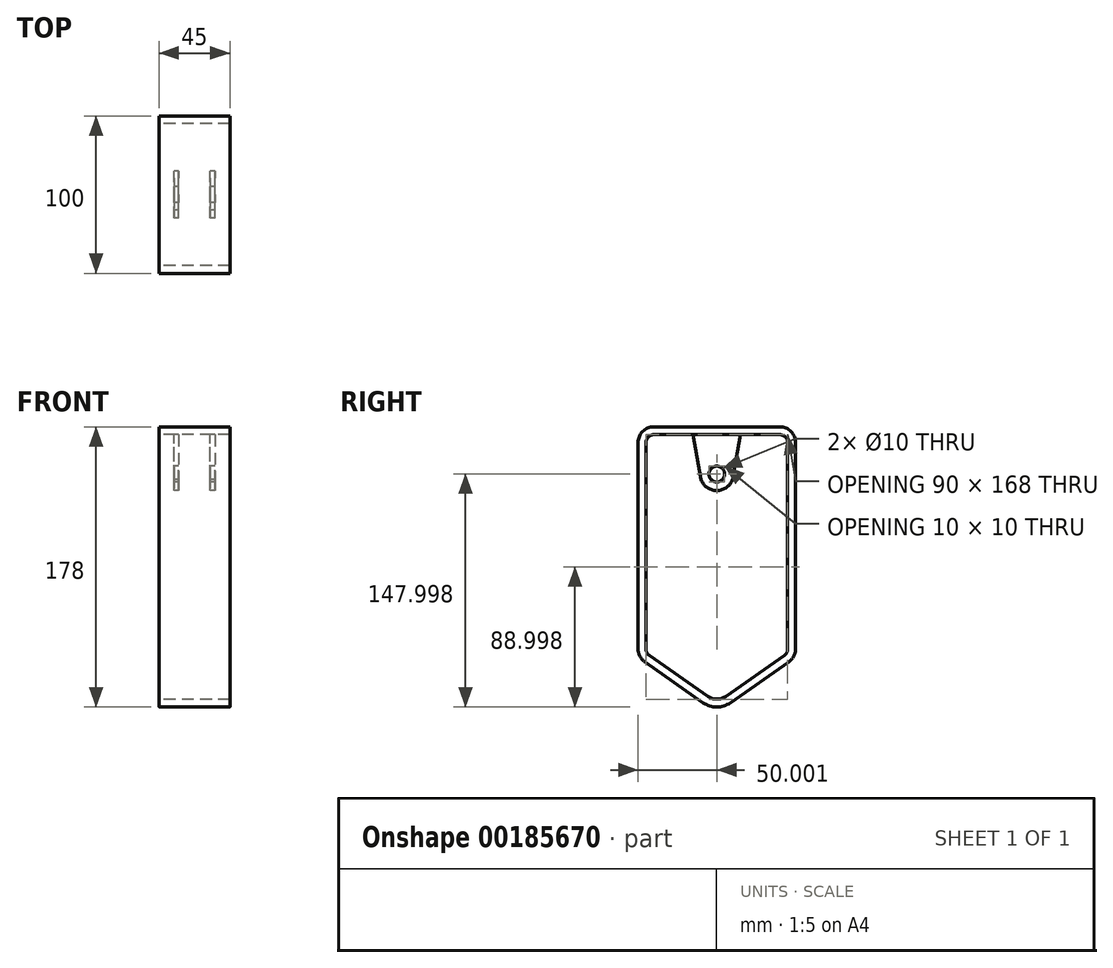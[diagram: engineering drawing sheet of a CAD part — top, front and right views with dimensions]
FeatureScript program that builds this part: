
annotation { "Feature Type Name" : "Feature", "Feature Type Description" : "" }
export const myFeature = defineFeature(function(context is Context, id is Id, definition is map)
    precondition{}
    {
        {
            var Q0;
            Q0=qCreatedBy(makeId("Right.planeOp"),FACE);
            var sketch = newSketch(context, id + "F0", { "sketchPlane" : qUnion([Q0])});
            skArc(sketch, "E0", {"start": v(-8.36, -11.33) * mm, "mid": v(0.24, -14.04) * mm, "end": v(8.84, -11.33) * mm});
            skArc(sketch, "E1", {"start": v(-5.5, -7.23) * mm, "mid": v(0.24, -9.04) * mm, "end": v(5.98, -7.23) * mm});
            skLineSegment(sketch, "E2", {"start": v(-45.5, 14.67) * mm, "end": v(-8.36, -11.33) * mm});
            skLineSegment(sketch, "E3", {"start": v(8.84, -11.33) * mm, "end": v(45.98, 14.67) * mm});
            skLineSegment(sketch, "E4.top", {"start": v(-39.76, 163.96) * mm, "end": v(40.24, 163.96) * mm});
            skLineSegment(sketch, "E4.left", {"start": v(-49.76, 22.86) * mm, "end": v(-49.76, 153.96) * mm});
            skLineSegment(sketch, "E4.right", {"start": v(50.24, 22.86) * mm, "end": v(50.24, 153.96) * mm});
            skPoint(sketch, "E4.middle", {"position": v(0, 50.92) * mm});
            skLineSegment(sketch, "E5.top", {"start": v(-39.76, 158.96) * mm, "end": v(40.24, 158.96) * mm});
            skLineSegment(sketch, "E5.left", {"start": v(-44.76, 22.86) * mm, "end": v(-44.76, 153.96) * mm});
            skLineSegment(sketch, "E5.right", {"start": v(45.24, 22.86) * mm, "end": v(45.24, 153.96) * mm});
            skLineSegment(sketch, "E6", {"start": v(-42.63, 18.77) * mm, "end": v(-5.5, -7.23) * mm});
            skLineSegment(sketch, "E7", {"start": v(43.1, 18.77) * mm, "end": v(5.98, -7.23) * mm});
            skPoint(sketch, "E7.endSnap0", {"position": v(29.76, 3.52) * mm});
            skPoint(sketch, "E8.orphan", {"position": v(21.33, 3.52) * mm});
            skArc(sketch, "E9.filletArc", {"start": v(-44.76, 22.86) * mm, "mid": v(-44.2, 20.55) * mm, "end": v(-42.63, 18.77) * mm});
            skArc(sketch, "E10.filletArc", {"start": v(43.1, 18.77) * mm, "mid": v(44.68, 20.55) * mm, "end": v(45.24, 22.86) * mm});
            skArc(sketch, "E11.filletArc", {"start": v(45.24, 153.96) * mm, "mid": v(43.78, 157.5) * mm, "end": v(40.24, 158.96) * mm});
            skArc(sketch, "E12.filletArc", {"start": v(-39.76, 158.96) * mm, "mid": v(-43.3, 157.5) * mm, "end": v(-44.76, 153.96) * mm});
            skArc(sketch, "E13.filletArc", {"start": v(-39.76, 163.96) * mm, "mid": v(-46.83, 161.03) * mm, "end": v(-49.76, 153.96) * mm});
            skArc(sketch, "E14.filletArc", {"start": v(50.24, 153.96) * mm, "mid": v(47.31, 161.03) * mm, "end": v(40.24, 163.96) * mm});
            skArc(sketch, "E15.filletArc", {"start": v(45.98, 14.67) * mm, "mid": v(49.11, 18.24) * mm, "end": v(50.24, 22.86) * mm});
            skArc(sketch, "E16.filletArc", {"start": v(-49.76, 22.86) * mm, "mid": v(-48.63, 18.24) * mm, "end": v(-45.5, 14.67) * mm});
            skCircle(sketch, "E17", {"center": v(0.24, 133.96) * mm, "radius": 5 * mm});
            skArc(sketch, "E18", {"start": v(-9.66, 130.45) * mm, "mid": v(1.13, 123.5) * mm, "end": v(10.59, 132.16) * mm});
            skLineSegment(sketch, "E19", {"start": v(-14.76, 158.96) * mm, "end": v(15.24, 158.96) * mm});
            skLineSegment(sketch, "E20", {"start": v(15.24, 158.96) * mm, "end": v(10.59, 132.16) * mm});
            skLineSegment(sketch, "E21.MirrorCS", {"start": v(-14.76, 158.96) * mm, "end": v(-9.66, 130.45) * mm});
            skSolve(sketch);
        }
        {
            var Q0;
            Q0 = qSketchRegion(id + "F0", true);
            var Q1;
            Q1=makeQuery(id+"F0.imprint","IMPRINT",FACE,{"disambiguationData":[TD([[makeQuery(id+"F0.imprint","IMPRINT",EDGE,{"derivedFrom":sQuery(id+"F0.wireOp",EDGE,"E17")}),-1.0]])]});
            extrude(context, id + "F1", {"entities" : qUnion([Q0, Q1]), "depth" : 45 * mm});
        }
        {
            var Q0;
            Q0=qCreatedBy(makeId("Front.planeOp"),FACE);
            var sketch = newSketch(context, id + "F2", { "sketchPlane" : qUnion([Q0])});
            skLineSegment(sketch, "E22.bottom", {"start": v(55.28, 158.96) * mm, "end": v(35.5, 158.96) * mm});
            skLineSegment(sketch, "E22.top", {"start": v(55.28, 116.97) * mm, "end": v(-7.3, 116.97) * mm});
            skLineSegment(sketch, "E22.left", {"start": v(55.28, 158.96) * mm, "end": v(55.28, 116.97) * mm});
            skLineSegment(sketch, "E22.right", {"start": v(-7.3, 158.96) * mm, "end": v(-7.3, 116.97) * mm});
            skLineSegment(sketch, "E23", {"start": v(35.5, 158.96) * mm, "end": v(35.5, 121.96) * mm});
            skLineSegment(sketch, "E24", {"start": v(32.5, 121.96) * mm, "end": v(32.5, 158.96) * mm});
            skLineSegment(sketch, "E25", {"start": v(35.5, 121.96) * mm, "end": v(32.5, 121.96) * mm});
            skLineSegment(sketch, "E26", {"start": v(12.5, 158.96) * mm, "end": v(12.5, 121.96) * mm});
            skLineSegment(sketch, "E27", {"start": v(12.5, 121.96) * mm, "end": v(9.5, 121.96) * mm});
            skLineSegment(sketch, "E28", {"start": v(9.5, 121.96) * mm, "end": v(9.5, 158.96) * mm});
            skLineSegment(sketch, "E29.trimOffspring", {"start": v(32.5, 158.96) * mm, "end": v(12.5, 158.96) * mm});
            skLineSegment(sketch, "E30.trimOffspring", {"start": v(9.5, 158.96) * mm, "end": v(-7.3, 158.96) * mm});
            skSolve(sketch);
        }
        {
            var Q0;
            Q0 = qSketchRegion(id + "F2", true);
            extrude(context, id + "F3", {"entities" : qUnion([Q0]), "operationType" : NewBodyOperationType.REMOVE, "endBound" : BoundingType.SYMMETRIC, "depth" : 50 * mm});
        }
    });
